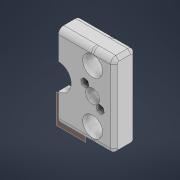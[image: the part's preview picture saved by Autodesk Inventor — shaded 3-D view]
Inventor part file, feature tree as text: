
AUTODESK INVENTOR PART (.ipt)
format: ipt  version: 2022 (Build 260153000, 153)  size: 292,352 bytes
history: native  units: mm
features: sketch x16, extrude x13, plane x2, fillet x2, chamfer x1
ambient origin geometry x8: Origin, YZ Plane, XZ Plane, XY Plane, X Axis, Y Axis, Z Axis, Center Point
bodies: Solid1 (feature_tree)
feature tree (34):
  extrude  "Extrusion1"  Depth=42.0mm
  extrude  "Extrusion2"  Depth=26.0mm
  extrude  "Extrusion4"  Depth=17.0mm TaperAngle=0.0deg
  extrude  "Extrusion5"  Depth=20.0mm
  plane  "Work Plane1"
  extrude  "Extrusion8"  Depth=15.1mm
  extrude  "Extrusion9"  Depth=10.0mm
  extrude  "Extrusion10"  TaperAngle=135.0deg  [1 undecoded]
  plane  "Work Plane2"
  extrude  "Extrusion11"  Depth=3.5mm
  extrude  "Extrusion12"  Depth=17.0mm TaperAngle=0.0deg
  extrude  "Extrusion13"  Depth=10.0mm TaperAngle=0.0deg
  fillet  "Fillet1"  Radius=25.0mm
  sketch  "Sketch14"  dims[d40=4.0mm d41=0.0mm d42=3.2mm]
  extrude  "Extrusion14"  Depth=4.0mm
  extrude  "Extrusion15"  [1 undecoded]
  sketch  "Sketch19"  dims[d53=18.0mm d54=0.0mm]
  sketch  "Sketch20"  dims[d55=2.0mm]
  fillet  "Fillet2"  Radius=2.75mm
  extrude  "Extrusion16"  Depth=2.75mm TaperAngle=0.0deg
  chamfer  "Chamfer1"  Distance=5.0mm
  sketch  "Sketch1"  dims[d0=42.0mm d1=63.0mm]
  sketch  "Sketch2"  dims[d2=17.0mm d3=0.0mm d4=26.0mm]
  sketch  "Sketch4"  dims[d5=10.5mm d6=17.0mm d7=0.0mm]
  sketch  "Sketch5"  dims[d14=20.0mm d15=20.0mm]
  sketch  "Sketch8"  dims[d16=15.1mm d17=15.1mm]
  sketch  "Sketch9"  dims[d18=17.0mm d19=0.0mm d21=10.0mm]
  sketch  "Sketch10"  dims[d22=8.25mm d23=135.0deg]
  sketch  "Sketch11"  dims[d24=16.5mm d25=3.5mm]
  sketch  "Sketch12"  dims[d26=3.5mm d27=17.0mm d28=0.0mm]
  sketch  "Sketch13"  dims[d36=19.5mm d37=10.0mm d38=0.0mm d39=25.0mm]
  sketch  "Sketch15"  dims[d43=10.0mm d44=0.0mm d45=-3.0mm d46=2.75mm]
  sketch  "Sketch17"  dims[d47=2.75mm d48=2.5mm d49=0.0mm d50=5.0mm d51=0.0mm]
  sketch  "Sketch21"  dims[d59=8.0mm d60=5.0mm d61=3.2mm d63=15.0mm d64=0.0mm d68=2.75mm d69=5.0mm d70=0.0mm d71=8.0mm d72=5.0mm d73=3.2mm d76=2.75mm d77=4.0mm d78=2.75mm d79=135.0deg d80=2.75mm d81=5.0mm d82=0.0mm d83=4.0mm d84=2.5mm d85=2.0mm d86=45.0deg]
note: 2 required parameter values undecoded (feature->parameter linkage not recoverable at this tier; creation-order binding heuristic only, values carry confidence <= 0.55)
